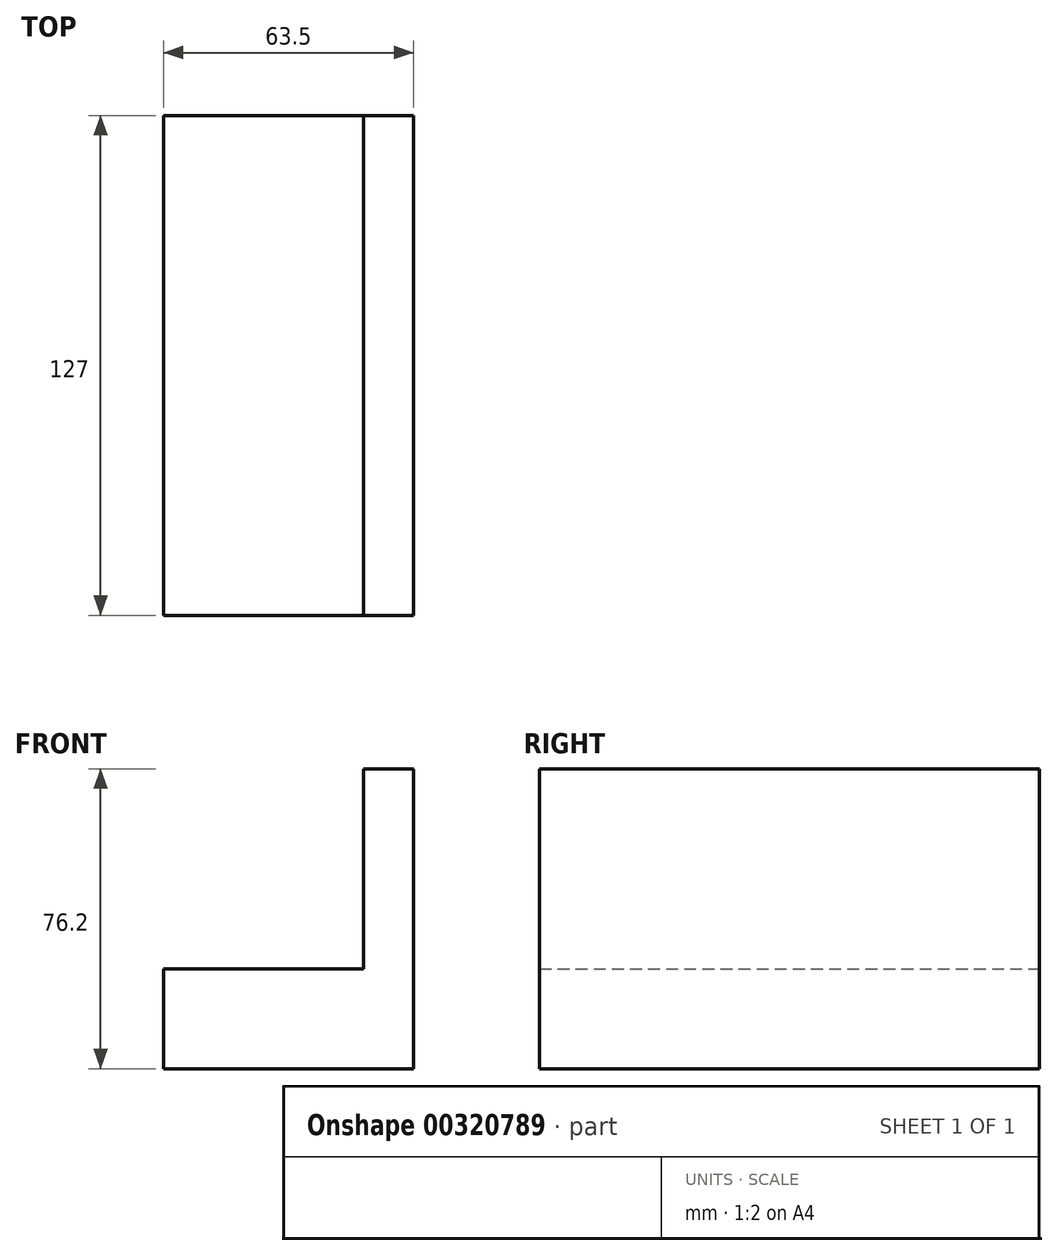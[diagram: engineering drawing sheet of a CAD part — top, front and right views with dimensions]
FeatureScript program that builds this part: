
annotation { "Feature Type Name" : "Feature", "Feature Type Description" : "" }
export const myFeature = defineFeature(function(context is Context, id is Id, definition is map)
    precondition{}
    {
        {
            var Q0;
            Q0=qCreatedBy(makeId("Front.planeOp"),FACE);
            var sketch = newSketch(context, id + "F0", { "sketchPlane" : qUnion([Q0])});
            skLineSegment(sketch, "E0", {"start": v(-31.9, -12.47) * mm, "end": v(-31.9, -37.87) * mm});
            skLineSegment(sketch, "E1", {"start": v(-31.9, -37.87) * mm, "end": v(31.6, -37.87) * mm});
            skLineSegment(sketch, "E2", {"start": v(31.6, -37.87) * mm, "end": v(31.6, 38.33) * mm});
            skLineSegment(sketch, "E3", {"start": v(31.6, 38.33) * mm, "end": v(-6.5, 38.33) * mm});
            skLineSegment(sketch, "E4", {"start": v(-6.5, 38.33) * mm, "end": v(-6.5, -12.47) * mm});
            skLineSegment(sketch, "E5", {"start": v(-6.5, -12.47) * mm, "end": v(-31.9, -12.47) * mm});
            skSolve(sketch);
        }
        {
            var Q0;
            Q0 = qSketchRegion(id + "F0", true);
            extrude(context, id + "F1", {"entities" : qUnion([Q0]), "depth" : 25.4 * mm});
        }
        {
            var Q0;
            Q0=makeQuery(id+"F1.opExtrude","CAP_FACE",FACE,{"disambiguationData":[OSD([sQuery(id+"F0.wireOp",EDGE,"E0"),sQuery(id+"F0.wireOp",EDGE,"E1"),sQuery(id+"F0.wireOp",EDGE,"E2"),sQuery(id+"F0.wireOp",EDGE,"E3"),sQuery(id+"F0.wireOp",EDGE,"E4"),sQuery(id+"F0.wireOp",EDGE,"E5")])],"isStart":false});
            extrude(context, id + "F2", {"entities" : qUnion([Q0]), "operationType" : NewBodyOperationType.ADD, "depth" : 101.6 * mm});
        }
        {
            var Q0;
            {var subQ0=sQuery(id+"F0.wireOp",EDGE,"E4");Q0=makeQuery(id+"F2.boolean.opBoolean","MERGE",FACE,{"derivedFrom":[makeQuery(id+"F1.opExtrude","SWEPT_FACE",FACE,{"disambiguationData":[OSD([subQ0])]}),makeQuery(id+"F2.opExtrude","SWEPT_FACE",FACE,{"disambiguationData":[OSD([subQ0])]})]});}
            var sketch = newSketch(context, id + "F3", { "sketchPlane" : qUnion([Q0])});
            skSolve(sketch);
        }
        {
            var Q0;
            {var subQ0=sQuery(id+"F0.wireOp",EDGE,"E4");Q0=makeQuery(id+"F3.imprint","IMPRINT",FACE,{"disambiguationData":[TD([[makeQuery(id+"F3.imprint","IMPRINT",EDGE,{"derivedFrom":makeQuery(id+"F1.opExtrude","CAP_EDGE",EDGE,{"disambiguationData":[OSD([subQ0])],"isStart":true})}),1.0]])]});}
            var sketch = newSketch(context, id + "F4", { "sketchPlane" : qUnion([Q0])});
            skLineSegment(sketch, "E6", {"start": v(38.46, 37.93) * mm, "end": v(38.46, 4.33) * mm});
            skLineSegment(sketch, "E7", {"start": v(38.46, 4.33) * mm, "end": v(85.15, 4.33) * mm});
            skLineSegment(sketch, "E8", {"start": v(85.15, 4.33) * mm, "end": v(85.15, 36.74) * mm});
            skLineSegment(sketch, "E9", {"start": v(38.46, 37.93) * mm, "end": v(85.15, 37.93) * mm});
            skSolve(sketch);
        }
        {
            var Q0;
            Q0 = qSketchRegion(id + "F4", true);
            var Q1;
            {var subQ0=sQuery(id+"F0.wireOp",EDGE,"E4");Q1=makeQuery(id+"F3.imprint","IMPRINT",FACE,{"disambiguationData":[TD([[makeQuery(id+"F3.imprint","IMPRINT",EDGE,{"derivedFrom":makeQuery(id+"F1.opExtrude","CAP_EDGE",EDGE,{"disambiguationData":[OSD([subQ0])],"isStart":true})}),1.0]])]});}
            extrude(context, id + "F5", {"entities" : qUnion([Q0, Q1]), "operationType" : NewBodyOperationType.REMOVE, "oppositeDirection" : true, "depth" : 25.4 * mm});
        }
    });
